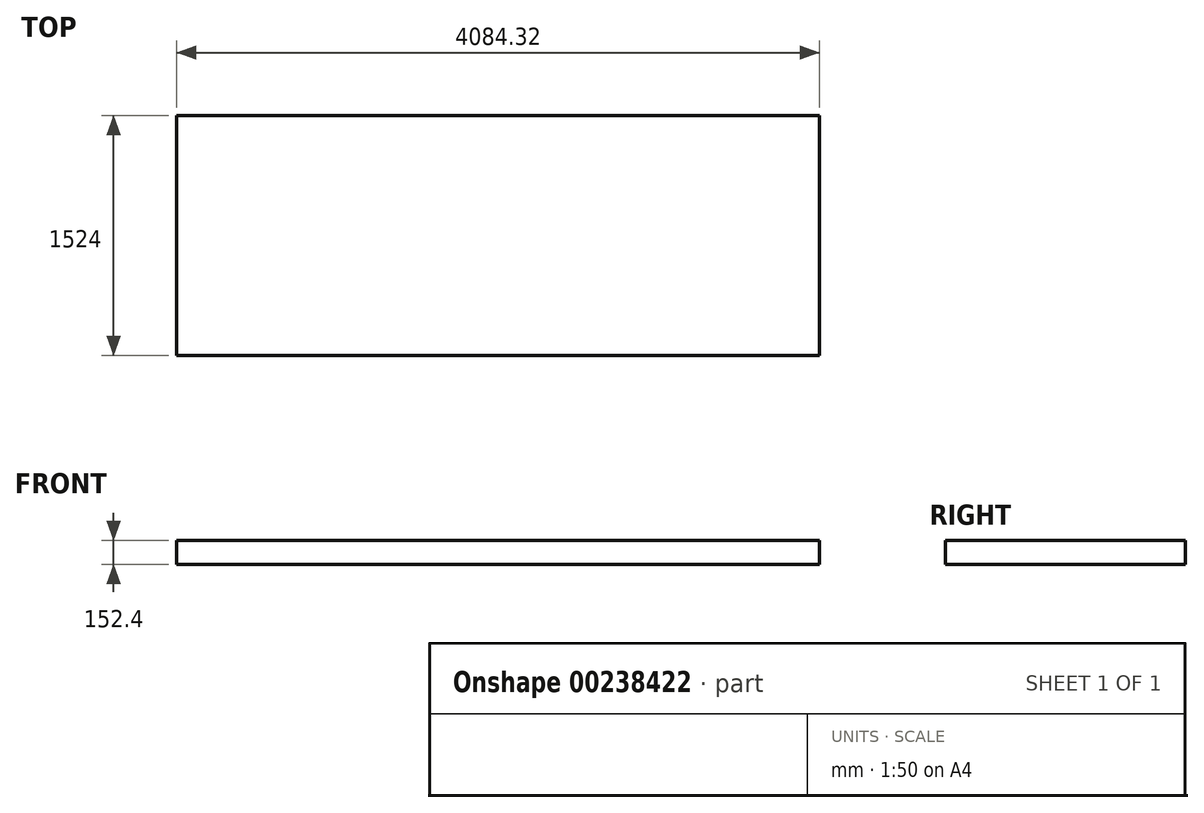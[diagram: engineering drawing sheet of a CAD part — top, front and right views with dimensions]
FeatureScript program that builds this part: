
annotation { "Feature Type Name" : "Feature", "Feature Type Description" : "" }
export const myFeature = defineFeature(function(context is Context, id is Id, definition is map)
    precondition{}
    {
        {
            var Q0;
            Q0=qCreatedBy(makeId("Top.planeOp"),FACE);
            var sketch = newSketch(context, id + "F0", { "sketchPlane" : qUnion([Q0])});
            skLineSegment(sketch, "E0.bottom", {"start": v(-167.4, 1450.88) * mm, "end": v(3916.92, 1450.88) * mm});
            skLineSegment(sketch, "E0.top", {"start": v(-167.4, -73.12) * mm, "end": v(3916.92, -73.12) * mm});
            skLineSegment(sketch, "E0.left", {"start": v(-167.4, 1450.88) * mm, "end": v(-167.4, -73.12) * mm});
            skLineSegment(sketch, "E0.right", {"start": v(3916.92, 1450.88) * mm, "end": v(3916.92, -73.12) * mm});
            skSolve(sketch);
        }
        {
            var Q0;
            Q0=makeQuery(id+"F0.imprint","IMPRINT",FACE,{"disambiguationData":[TD([[makeQuery(id+"F0.imprint","IMPRINT",EDGE,{"derivedFrom":sQuery(id+"F0.wireOp",EDGE,"E0.bottom")}),-1.0]])]});
            extrude(context, id + "F1", {"entities" : qUnion([Q0]), "oppositeDirection" : true, "depth" : 152.4 * mm});
        }
    });
